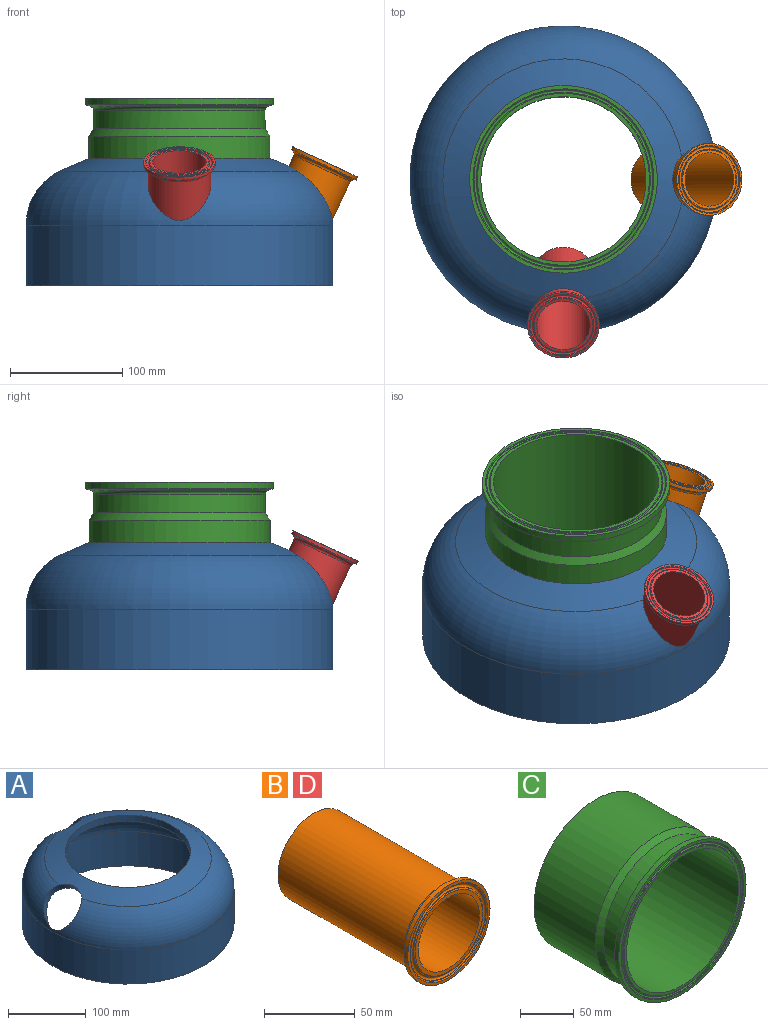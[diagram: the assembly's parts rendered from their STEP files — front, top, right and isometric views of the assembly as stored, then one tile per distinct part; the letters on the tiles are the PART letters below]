
ASSEMBLY  parts=4 mates=3
PART A: 11 faces, bbox 295.6x295.6x112.9 mm
  f0: torus R=83.22mm, axis (0,0,-1), area 6606.4mm2, adj f1,f2,f5,f10
  f1: cylinder r=27.94mm len=71.24mm, axis (0.42,0,-0.91), area 2277.8mm2, adj f0,f2,f3,f4,f5,f8
  f2: sphere r=229.06mm, area 13515mm2, adj f0,f1,f4,f9,f10
  f3: sphere r=238.33mm, area 16454.2mm2, adj f1,f8,f9,f10
  f4: torus R=83.22mm, axis (0,0,-1), area 24757.6mm2, adj f1,f2,f5,f10
  f5: cylinder r=127.25mm len=254.51mm, axis (0,0,-1), area 42284.4mm2, adj f0,f1,f4,f6,f10
  f6: plane 273.05x273.05mm, normal (0,0,-1), area 7682.7mm2, adj f5,f7
  f7: cylinder r=136.53mm len=273.05mm, axis (0,0,-1), area 46258.1mm2, adj f6,f8
  f8: torus R=83.22mm, axis (0,0,-1), area 41689mm2, adj f1,f3,f7,f10
  f9: cylinder r=80.64mm len=161.29mm, axis (0,0,-1), area 5005.3mm2, adj f2,f3
  f10: cylinder r=27.94mm len=71.24mm, axis (0,-0.42,-0.91), area 2278.2mm2, adj f0,f2,f3,f4,f5,f8
PART B: 13 faces, bbox 67.1x105x67.1 mm
  f0: cylinder r=31.95mm len=63.91mm, axis (0,-1,0), area 571.1mm2, adj f1,f10
  f1: cone r=29.93mm half-angle=70deg, axis (0,-1,0), area 419.1mm2, adj f0,f2
  f2: torus R=31.01mm, axis (0,-1,0), area 696.4mm2, adj f1,f3
  f3: cylinder r=27.84mm len=98.44mm, axis (0,-1,0), area 17218.2mm2, adj f2,f12
  f4: cylinder r=23.75mm len=105mm, axis (0,-1,0), area 15668.6mm2, adj f11,f12
  f5: torus R=26.18mm, axis (0,-1,0), area 153.8mm2, adj f6,f11
  f6: cone r=27.07mm half-angle=23deg, axis (0,1,0), area 72.4mm2, adj f5,f7
  f7: torus R=28.17mm, axis (0,-1,0), area 494.2mm2, adj f6,f8
  f8: cone r=29.43mm half-angle=23deg, axis (0,-1,0), area 78.8mm2, adj f7,f9
  f9: torus R=30.16mm, axis (0,-1,0), area 172.1mm2, adj f8,f10
  f10: plane 63.91x63.91mm, normal (0,-1,0), area 350.1mm2, adj f0,f9
  f11: plane 52.36x52.36mm, normal (0,-1,0), area 381mm2, adj f4,f5
  f12: plane 55.68x55.68mm, normal (0,1,0), area 662.8mm2, adj f3,f4
PART C: 15 faces, bbox 174.1x114.3x174.1 mm
  f0: cylinder r=76.2mm len=152.4mm, axis (0,-1,0), area 8023.1mm2, adj f9,f14
  f1: plane 166.88x166.88mm, normal (0,-1,0), area 1551.2mm2, adj f2,f11
  f2: torus R=80.43mm, axis (0,-1,0), area 462.9mm2, adj f1,f3
  f3: cone r=79.7mm half-angle=23deg, axis (0,-1,0), area 213.6mm2, adj f2,f4
  f4: torus R=78.44mm, axis (0,-1,0), area 1376mm2, adj f3,f5
  f5: cone r=77.34mm half-angle=23deg, axis (0,1,0), area 207.3mm2, adj f4,f6
  f6: torus R=76.44mm, axis (0,-1,0), area 444.6mm2, adj f5,f7
  f7: plane 152.89x152.89mm, normal (0,-1,0), area 1418.8mm2, adj f6,f8
  f8: cylinder r=73.43mm len=146.86mm, axis (0,-1,0), area 52736.1mm2, adj f7,f13
  f9: torus R=79.38mm, axis (0,-1,0), area 1875mm2, adj f0,f10
  f10: cone r=78.29mm half-angle=70deg, axis (0,-1,0), area 2784.5mm2, adj f9,f11
  f11: cylinder r=83.44mm len=166.88mm, axis (0,-1,0), area 2929.6mm2, adj f1,f10
  f12: cylinder r=80.54mm len=161.09mm, axis (0,-1,0), area 40863.4mm2, adj f13,f14
  f13: plane 161.09x161.09mm, normal (0,1,0), area 3440.3mm2, adj f8,f12
  f14: cone r=80.54mm half-angle=34.4deg, axis (0,1,0), area 3788.4mm2, adj f0,f12
PART D: same geometry as B
PLACE A rot(axis=(0,0,1),180deg) t=(0,0,0)mm
PLACE B rot(axis=(0.15,-0.7,0.7),162.4deg) t=(129.75,0,109.97)mm
PLACE C rot(axis=(0,-0.71,0.71),180deg) t=(0,0,166.56)mm
PLACE D rot(axis=(0,0.84,-0.54),180deg) t=(0,-129.75,109.97)mm
MATE fastened A.f1 <-> B.f0  axis (-0.42,0,-0.91) through (112.21,0,72.36)mm
MATE fastened A.f9 <-> C.f12  axis (0,0,-1) through (0,0,103.06)mm
MATE fastened A.f10 <-> D.f0  axis (0,0.42,-0.91) through (0,-112.21,72.36)mm
